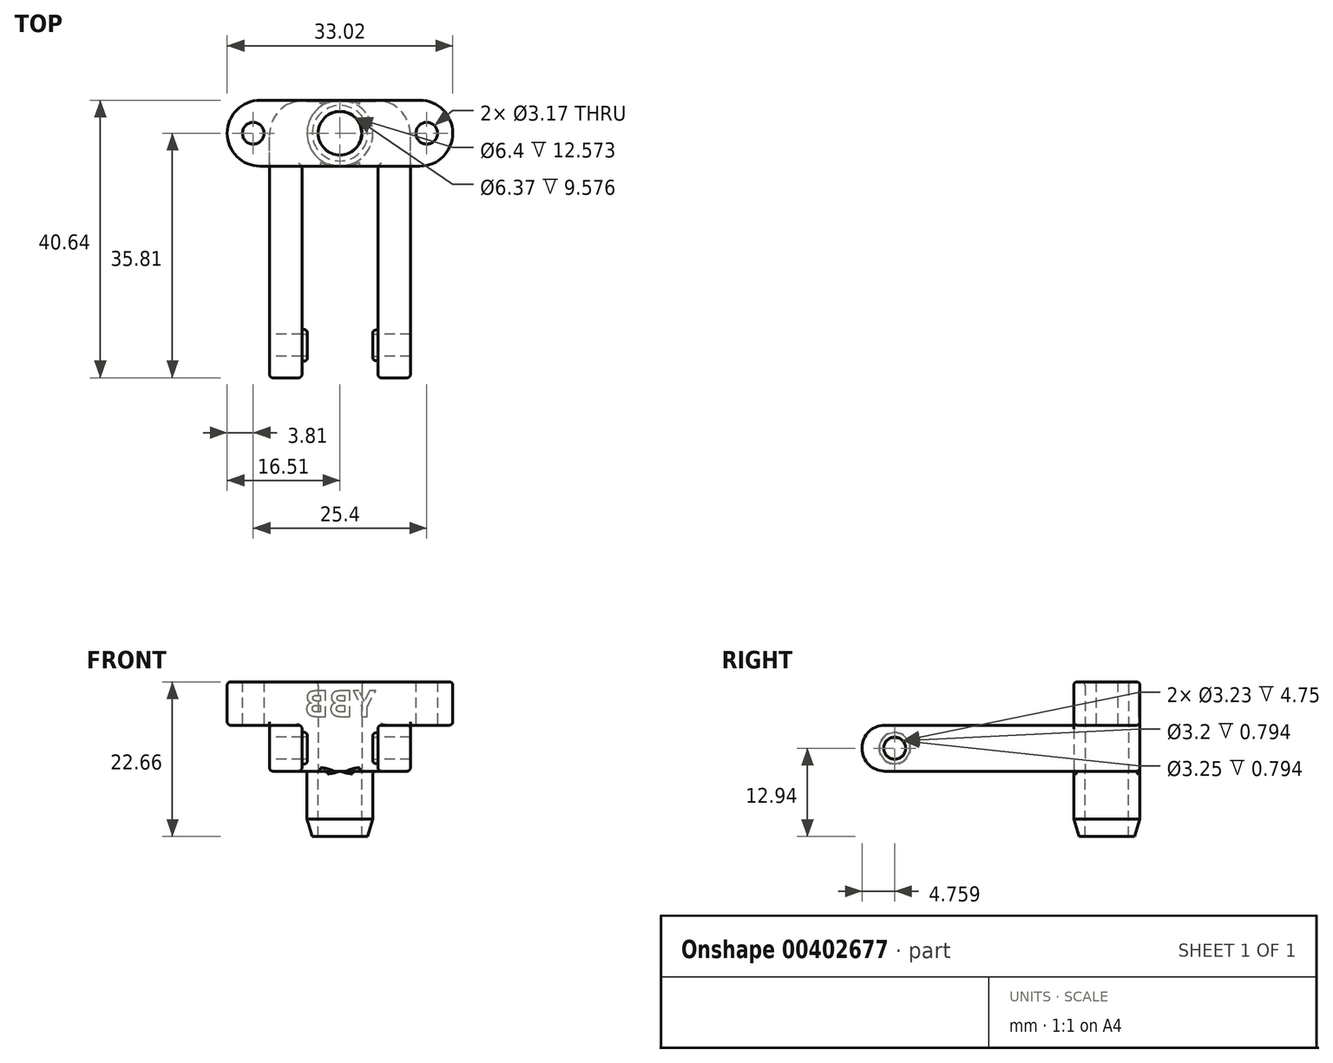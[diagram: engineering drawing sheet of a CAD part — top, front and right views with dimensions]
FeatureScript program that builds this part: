
annotation { "Feature Type Name" : "Feature", "Feature Type Description" : "" }
export const myFeature = defineFeature(function(context is Context, id is Id, definition is map)
    precondition{}
    {
        {
            var Q0;
            Q0=qCreatedBy(makeId("Top.planeOp"),FACE);
            var sketch = newSketch(context, id + "F0", { "sketchPlane" : qUnion([Q0])});
            skLineSegment(sketch, "E0.bottom", {"start": v(10.31, -4.83) * mm, "end": v(-10.31, -4.83) * mm});
            skLineSegment(sketch, "E0.top", {"start": v(10.31, 4.83) * mm, "end": v(-10.31, 4.83) * mm});
            skLineSegment(sketch, "E0.left", {"start": v(10.31, -4.83) * mm, "end": v(10.31, 4.83) * mm});
            skLineSegment(sketch, "E0.right", {"start": v(-10.31, -4.83) * mm, "end": v(-10.31, 4.83) * mm});
            skPoint(sketch, "E0.middle", {"position": v(0, 0) * mm});
            skCircle(sketch, "E1", {"center": v(0, 0) * mm, "radius": 3.2 * mm});
            skLineSegment(sketch, "E2.bottom", {"start": v(10.31, -4.83) * mm, "end": v(5.56, -4.83) * mm});
            skLineSegment(sketch, "E2.top", {"start": v(10.31, -35.81) * mm, "end": v(5.56, -35.81) * mm});
            skLineSegment(sketch, "E2.left", {"start": v(10.31, -4.83) * mm, "end": v(10.31, -35.81) * mm});
            skLineSegment(sketch, "E2.right", {"start": v(5.56, -4.83) * mm, "end": v(5.56, -35.81) * mm});
            skLineSegment(sketch, "E3.MirrorCS", {"start": v(-5.56, -4.83) * mm, "end": v(-5.56, -35.81) * mm});
            skLineSegment(sketch, "E4.MirrorCS", {"start": v(-10.31, -35.81) * mm, "end": v(-5.56, -35.81) * mm});
            skLineSegment(sketch, "E5.MirrorCS", {"start": v(-10.31, -4.83) * mm, "end": v(-10.31, -35.81) * mm});
            skSolve(sketch);
        }
        {
            var Q0;
            {var subQ8=sQuery(id+"F0.wireOp",EDGE,"E3.MirrorCS");Q0=qUnion([makeQuery(id+"F0.imprint","IMPRINT",FACE,{"disambiguationData":[TD([[makeQuery(id+"F0.imprint","IMPRINT",EDGE,{"derivedFrom":sQuery(id+"F0.wireOp",EDGE,"E0.top")}),1.0]])]}),makeQuery(id+"F0.imprint","IMPRINT",FACE,{"disambiguationData":[TD([[makeQuery(id+"F0.imprint","IMPRINT",EDGE,{"derivedFrom":subQ8}),-1.0]])]}),makeQuery(id+"F0.imprint","IMPRINT",FACE,{"disambiguationData":[TD([[makeQuery(id+"F0.imprint","IMPRINT",EDGE,{"derivedFrom":sQuery(id+"F0.wireOp",EDGE,"E2.top")}),-1.0]])]})]);}
            extrude(context, id + "F1", {"entities" : qUnion([Q0]), "endBound" : BoundingType.SYMMETRIC, "depth" : 6.73 * mm});
        }
        {
            var Q0;
            Q0=makeQuery(id+"F1.opExtrude","CAP_FACE",FACE,{"disambiguationData":[OSD([sQuery(id+"F0.wireOp",EDGE,"E0.bottom"),sQuery(id+"F0.wireOp",EDGE,"E0.top"),sQuery(id+"F0.wireOp",EDGE,"E0.left"),sQuery(id+"F0.wireOp",EDGE,"E0.right"),sQuery(id+"F0.wireOp",EDGE,"E1"),sQuery(id+"F0.wireOp",EDGE,"E2.top"),sQuery(id+"F0.wireOp",EDGE,"E2.left"),sQuery(id+"F0.wireOp",EDGE,"E2.right"),sQuery(id+"F0.wireOp",EDGE,"E3.MirrorCS"),sQuery(id+"F0.wireOp",EDGE,"E4.MirrorCS"),sQuery(id+"F0.wireOp",EDGE,"E5.MirrorCS")])],"isStart":true});
            var sketch = newSketch(context, id + "F2", { "sketchPlane" : qUnion([Q0])});
            skCircle(sketch, "E6", {"center": v(0, 0) * mm, "radius": 4.83 * mm});
            skCircle(sketch, "E7", {"center": v(0, 0) * mm, "radius": 3.15 * mm});
            skSolve(sketch);
        }
        {
            var Q0;
            Q0=makeQuery(id+"F1.opExtrude","SWEPT_FACE",FACE,{"disambiguationData":[OSD([sQuery(id+"F0.wireOp",EDGE,"E0.right"),sQuery(id+"F0.wireOp",EDGE,"E5.MirrorCS")])]});
            var sketch = newSketch(context, id + "F3", { "sketchPlane" : qUnion([Q0])});
            skCircle(sketch, "E8", {"center": v(31.05, 0) * mm, "radius": 1.61 * mm});
            skSolve(sketch);
        }
        {
            var Q0;
            Q0 = qSketchRegion(id + "F3", true);
            extrude(context, id + "F4", {"entities" : qUnion([Q0]), "operationType" : NewBodyOperationType.REMOVE, "endBound" : BoundingType.THROUGH_ALL, "oppositeDirection" : true, "depth" : 25.4 * mm});
        }
        {
            var Q0;
            Q0 = qSketchRegion(id + "F2", true);
            extrude(context, id + "F5", {"entities" : qUnion([Q0]), "operationType" : NewBodyOperationType.ADD, "depth" : 9.58 * mm});
        }
        {
            var Q0;
            Q0=makeQuery(id+"F1.opExtrude","SWEPT_FACE",FACE,{"disambiguationData":[OSD([sQuery(id+"F0.wireOp",EDGE,"E3.MirrorCS")])]});
            var sketch = newSketch(context, id + "F6", { "sketchPlane" : qUnion([Q0])});
            skCircle(sketch, "E9", {"center": v(-31.05, 0) * mm, "radius": 1.6 * mm});
            skCircle(sketch, "E10", {"center": v(-31.05, 0) * mm, "radius": 2.32 * mm});
            skSolve(sketch);
        }
        {
            var Q0;
            Q0 = qSketchRegion(id + "F6", true);
            extrude(context, id + "F7", {"entities" : qUnion([Q0]), "operationType" : NewBodyOperationType.ADD, "depth" : 0.8 * mm});
        }
        {
            var Q0;
            Q0=makeQuery(id+"F1.opExtrude","SWEPT_FACE",FACE,{"disambiguationData":[OSD([sQuery(id+"F0.wireOp",EDGE,"E2.right")])]});
            var sketch = newSketch(context, id + "F8", { "sketchPlane" : qUnion([Q0])});
            skCircle(sketch, "E11", {"center": v(31.05, 0) * mm, "radius": 1.62 * mm});
            skCircle(sketch, "E12", {"center": v(31.05, 0) * mm, "radius": 2.25 * mm});
            skSolve(sketch);
        }
        {
            var Q0;
            Q0 = qSketchRegion(id + "F8", true);
            extrude(context, id + "F9", {"entities" : qUnion([Q0]), "operationType" : NewBodyOperationType.ADD, "depth" : 0.8 * mm});
        }
        {
            var Q0;
            Q0=makeQuery(id+"F1.opExtrude","CAP_FACE",FACE,{"disambiguationData":[OSD([sQuery(id+"F0.wireOp",EDGE,"E0.bottom"),sQuery(id+"F0.wireOp",EDGE,"E0.top"),sQuery(id+"F0.wireOp",EDGE,"E0.left"),sQuery(id+"F0.wireOp",EDGE,"E0.right"),sQuery(id+"F0.wireOp",EDGE,"E1"),sQuery(id+"F0.wireOp",EDGE,"E2.top"),sQuery(id+"F0.wireOp",EDGE,"E2.left"),sQuery(id+"F0.wireOp",EDGE,"E2.right"),sQuery(id+"F0.wireOp",EDGE,"E3.MirrorCS"),sQuery(id+"F0.wireOp",EDGE,"E4.MirrorCS"),sQuery(id+"F0.wireOp",EDGE,"E5.MirrorCS")])],"isStart":false});
            var sketch = newSketch(context, id + "F10", { "sketchPlane" : qUnion([Q0])});
            skLineSegment(sketch, "E13.bottom", {"start": v(16.51, -4.83) * mm, "end": v(-16.51, -4.83) * mm});
            skLineSegment(sketch, "E13.top", {"start": v(16.51, 4.83) * mm, "end": v(-16.51, 4.83) * mm});
            skLineSegment(sketch, "E13.left", {"start": v(16.51, -4.83) * mm, "end": v(16.51, 4.83) * mm});
            skLineSegment(sketch, "E13.right", {"start": v(-16.51, -4.83) * mm, "end": v(-16.51, 4.83) * mm});
            skPoint(sketch, "E13.middle", {"position": v(0, 0) * mm});
            skCircle(sketch, "E14", {"center": v(0, 0) * mm, "radius": 3.2 * mm});
            skCircle(sketch, "E15", {"center": v(12.7, 0) * mm, "radius": 1.59 * mm});
            skCircle(sketch, "E16.MirrorC", {"center": v(-12.7, 0) * mm, "radius": 1.59 * mm});
            skSolve(sketch);
        }
        {
            var Q0;
            Q0 = qSketchRegion(id + "F10", true);
            extrude(context, id + "F11", {"entities" : qUnion([Q0]), "operationType" : NewBodyOperationType.ADD, "depth" : 6.35 * mm});
        }
        {
            var Q0;
            Q0=makeQuery(id+"F11.opExtrude","CAP_EDGE",EDGE,{"disambiguationData":[OSD([sQuery(id+"F10.wireOp",EDGE,"E13.left")])],"isStart":false});
            var Q1;
            Q1=makeQuery(id+"F11.opExtrude","CAP_EDGE",EDGE,{"disambiguationData":[OSD([sQuery(id+"F10.wireOp",EDGE,"E13.top")])],"isStart":false});
            var Q2;
            Q2=makeQuery(id+"F11.opExtrude","CAP_EDGE",EDGE,{"disambiguationData":[OSD([sQuery(id+"F10.wireOp",EDGE,"E13.right")])],"isStart":false});
            var Q3;
            Q3=makeQuery(id+"F11.opExtrude","CAP_EDGE",EDGE,{"disambiguationData":[OSD([sQuery(id+"F10.wireOp",EDGE,"E13.bottom")])],"isStart":false});
            var Q4;
            Q4=makeQuery(id+"F11.opExtrude","CAP_EDGE",EDGE,{"disambiguationData":[OSD([sQuery(id+"F10.wireOp",EDGE,"E14")])],"isStart":false});
            var Q5;
            {var subQ2=sQuery(id+"F0.wireOp",EDGE,"E0.bottom");var subQ3=sQuery(id+"F10.wireOp",EDGE,"E13.bottom");var subQ4=makeQuery(id+"F11.opExtrude","SWEPT_FACE",FACE,{"disambiguationData":[OSD([subQ3])]});var subQ5=makeQuery(id+"F1.opExtrude","SWEPT_FACE",FACE,{"disambiguationData":[OSD([subQ2])]});var subQ6=sQuery(id+"F10.wireOp",EDGE,"E13.right");var subQ7=makeQuery(id+"F11.opExtrude","CAP_FACE",FACE,{"disambiguationData":[OSD([subQ3,sQuery(id+"F10.wireOp",EDGE,"E13.top"),sQuery(id+"F10.wireOp",EDGE,"E13.left"),subQ6,sQuery(id+"F10.wireOp",EDGE,"E14"),sQuery(id+"F10.wireOp",EDGE,"E15"),sQuery(id+"F10.wireOp",EDGE,"E16.MirrorC")])],"isStart":true});Q5=makeQuery(id+"F11.boolean.opBoolean","SPLIT",EDGE,{"disambiguationData":[topologyDisambiguationEdgeConnected([subQ5,subQ4,subQ7]),TD([makeQuery(id+"F11.opExtrude","SWEPT_FACE",FACE,{"disambiguationData":[OSD([subQ6])]})])],"derivedFrom":makeQuery(id+"F11.opExtrude","CAP_EDGE",EDGE,{"disambiguationData":[OSD([subQ3])],"isStart":true})});}
            var Q6;
            {var subQ2=sQuery(id+"F10.wireOp",EDGE,"E13.left");var subQ3=sQuery(id+"F10.wireOp",EDGE,"E13.bottom");var subQ4=makeQuery(id+"F11.opExtrude","CAP_FACE",FACE,{"disambiguationData":[OSD([subQ3,sQuery(id+"F10.wireOp",EDGE,"E13.top"),subQ2,sQuery(id+"F10.wireOp",EDGE,"E13.right"),sQuery(id+"F10.wireOp",EDGE,"E14"),sQuery(id+"F10.wireOp",EDGE,"E15"),sQuery(id+"F10.wireOp",EDGE,"E16.MirrorC")])],"isStart":true});var subQ5=sQuery(id+"F0.wireOp",EDGE,"E0.bottom");var subQ6=makeQuery(id+"F11.opExtrude","SWEPT_FACE",FACE,{"disambiguationData":[OSD([subQ3])]});var subQ7=makeQuery(id+"F1.opExtrude","SWEPT_FACE",FACE,{"disambiguationData":[OSD([subQ5])]});Q6=makeQuery(id+"F11.boolean.opBoolean","SPLIT",EDGE,{"disambiguationData":[topologyDisambiguationEdgeConnected([subQ7,subQ6,subQ4]),TD([makeQuery(id+"F11.opExtrude","SWEPT_FACE",FACE,{"disambiguationData":[OSD([subQ2])]})])],"derivedFrom":makeQuery(id+"F11.opExtrude","CAP_EDGE",EDGE,{"disambiguationData":[OSD([subQ3])],"isStart":true})});}
            var Q7;
            Q7=makeQuery(id+"F11.opExtrude","CAP_EDGE",EDGE,{"disambiguationData":[OSD([sQuery(id+"F10.wireOp",EDGE,"E13.left")])],"isStart":true});
            var Q8;
            {var subQ0=sQuery(id+"F10.wireOp",EDGE,"E13.top");var subQ1=sQuery(id+"F10.wireOp",EDGE,"E13.left");Q8=makeQuery(id+"F11.boolean.opBoolean","SPLIT",EDGE,{"disambiguationData":[TD([makeQuery(id+"F11.opExtrude","SWEPT_FACE",FACE,{"disambiguationData":[OSD([subQ1])]})])],"derivedFrom":makeQuery(id+"F11.opExtrude","CAP_EDGE",EDGE,{"disambiguationData":[OSD([subQ0])],"isStart":true})});}
            var Q9;
            {var subQ0=sQuery(id+"F10.wireOp",EDGE,"E13.top");var subQ1=sQuery(id+"F10.wireOp",EDGE,"E13.right");Q9=makeQuery(id+"F11.boolean.opBoolean","SPLIT",EDGE,{"disambiguationData":[TD([makeQuery(id+"F11.opExtrude","SWEPT_FACE",FACE,{"disambiguationData":[OSD([subQ1])]})])],"derivedFrom":makeQuery(id+"F11.opExtrude","CAP_EDGE",EDGE,{"disambiguationData":[OSD([subQ0])],"isStart":true})});}
            var Q10;
            Q10=makeQuery(id+"F11.opExtrude","CAP_EDGE",EDGE,{"disambiguationData":[OSD([sQuery(id+"F10.wireOp",EDGE,"E13.right")])],"isStart":true});
            fillet(context, id + "F12", {"entities" : qUnion([Q0, Q1, Q2, Q3, Q4, Q5, Q6, Q7, Q8, Q9, Q10]), "radius" : 0.5 * mm, "allowEdgeOverflow" : false});
        }
        {
            var Q0;
            Q0=makeQuery(id+"F1.opExtrude","CAP_EDGE",EDGE,{"disambiguationData":[OSD([sQuery(id+"F0.wireOp",EDGE,"E3.MirrorCS")])],"isStart":false});
            var Q1;
            Q1=makeQuery(id+"F7.opExtrude","CAP_EDGE",EDGE,{"disambiguationData":[OSD([sQuery(id+"F6.wireOp",EDGE,"E10")])],"isStart":false});
            var Q2;
            Q2=makeQuery(id+"F1.opExtrude","CAP_EDGE",EDGE,{"disambiguationData":[OSD([sQuery(id+"F0.wireOp",EDGE,"E2.right")])],"isStart":false});
            var Q3;
            Q3=makeQuery(id+"F9.opExtrude","CAP_EDGE",EDGE,{"disambiguationData":[OSD([sQuery(id+"F8.wireOp",EDGE,"E12")])],"isStart":false});
            fillet(context, id + "F13", {"entities" : qUnion([Q0, Q1, Q2, Q3]), "radius" : 0.5 * mm, "tangentPropagation" : true, "allowEdgeOverflow" : false});
        }
        {
            var Q0;
            Q0=makeQuery(id+"F5.boolean.opBoolean","SPLIT",EDGE,{"disambiguationData":[OD(0.0)],"derivedFrom":makeQuery(id+"F5.opExtrude","CAP_EDGE",EDGE,{"disambiguationData":[OSD([sQuery(id+"F2.wireOp",EDGE,"E6")])],"isStart":true})});
            var Q1;
            Q1=makeQuery(id+"F5.boolean.opBoolean","SPLIT",EDGE,{"disambiguationData":[OD(1.0)],"derivedFrom":makeQuery(id+"F5.opExtrude","CAP_EDGE",EDGE,{"disambiguationData":[OSD([sQuery(id+"F2.wireOp",EDGE,"E6")])],"isStart":true})});
            fillet(context, id + "F14", {"entities" : qUnion([Q0, Q1]), "radius" : 0.38 * mm, "tangentPropagation" : true, "allowEdgeOverflow" : false});
        }
        {
            var Q0;
            Q0=makeQuery(id+"F1.opExtrude","SWEPT_EDGE",EDGE,{"disambiguationData":[OSD([sQuery(id+"F0.wireOp",EDGE,"E3.MirrorCS"),sQuery(id+"F0.wireOp",EDGE,"E4.MirrorCS")])]});
            var Q1;
            Q1=makeQuery(id+"F1.opExtrude","SWEPT_EDGE",EDGE,{"disambiguationData":[OSD([sQuery(id+"F0.wireOp",EDGE,"E2.top"),sQuery(id+"F0.wireOp",EDGE,"E2.right")])]});
            var Q2;
            {var subQ0=sQuery(id+"F0.wireOp",EDGE,"E5.MirrorCS");var subQ1=sQuery(id+"F0.wireOp",EDGE,"E0.right");Q2=makeQuery(id+"F11.boolean.opBoolean","SPLIT",EDGE,{"disambiguationData":[topologyDisambiguationEdgeConnected([makeQuery(id+"F1.opExtrude","CAP_FACE",FACE,{"disambiguationData":[OSD([sQuery(id+"F0.wireOp",EDGE,"E0.bottom"),sQuery(id+"F0.wireOp",EDGE,"E0.top"),sQuery(id+"F0.wireOp",EDGE,"E0.left"),subQ1,sQuery(id+"F0.wireOp",EDGE,"E1"),sQuery(id+"F0.wireOp",EDGE,"E2.top"),sQuery(id+"F0.wireOp",EDGE,"E2.left"),sQuery(id+"F0.wireOp",EDGE,"E2.right"),sQuery(id+"F0.wireOp",EDGE,"E3.MirrorCS"),sQuery(id+"F0.wireOp",EDGE,"E4.MirrorCS"),subQ0])],"isStart":false})])],"derivedFrom":makeQuery(id+"F1.opExtrude","CAP_EDGE",EDGE,{"disambiguationData":[OSD([subQ1,subQ0])],"isStart":false})});}
            var Q3;
            Q3=makeQuery(id+"F1.opExtrude","SWEPT_EDGE",EDGE,{"disambiguationData":[OSD([sQuery(id+"F0.wireOp",EDGE,"E4.MirrorCS"),sQuery(id+"F0.wireOp",EDGE,"E5.MirrorCS")])]});
            var Q4;
            Q4=makeQuery(id+"F1.opExtrude","CAP_EDGE",EDGE,{"disambiguationData":[OSD([sQuery(id+"F0.wireOp",EDGE,"E0.right"),sQuery(id+"F0.wireOp",EDGE,"E5.MirrorCS")])],"isStart":true});
            var Q5;
            {var subQ0=sQuery(id+"F0.wireOp",EDGE,"E5.MirrorCS");var subQ1=sQuery(id+"F0.wireOp",EDGE,"E0.right");var subQ2=sQuery(id+"F0.wireOp",EDGE,"E0.top");Q5=makeQuery(id+"F5.boolean.opBoolean","SPLIT",EDGE,{"disambiguationData":[TD([makeQuery(id+"F1.opExtrude","SWEPT_FACE",FACE,{"disambiguationData":[OSD([subQ1,subQ0])]})])],"derivedFrom":makeQuery(id+"F1.opExtrude","CAP_EDGE",EDGE,{"disambiguationData":[OSD([subQ2])],"isStart":true})});}
            var Q6;
            {var subQ0=sQuery(id+"F0.wireOp",EDGE,"E2.left");var subQ1=sQuery(id+"F0.wireOp",EDGE,"E0.left");var subQ2=sQuery(id+"F0.wireOp",EDGE,"E0.top");Q6=makeQuery(id+"F5.boolean.opBoolean","SPLIT",EDGE,{"disambiguationData":[TD([makeQuery(id+"F1.opExtrude","SWEPT_FACE",FACE,{"disambiguationData":[OSD([subQ1,subQ0])]})])],"derivedFrom":makeQuery(id+"F1.opExtrude","CAP_EDGE",EDGE,{"disambiguationData":[OSD([subQ2])],"isStart":true})});}
            var Q7;
            {var subQ0=sQuery(id+"F0.wireOp",EDGE,"E0.bottom");var subQ1=sQuery(id+"F0.wireOp",EDGE,"E3.MirrorCS");Q7=makeQuery(id+"F5.boolean.opBoolean","SPLIT",EDGE,{"disambiguationData":[TD([makeQuery(id+"F1.opExtrude","SWEPT_FACE",FACE,{"disambiguationData":[OSD([subQ1])]})])],"derivedFrom":makeQuery(id+"F1.opExtrude","CAP_EDGE",EDGE,{"disambiguationData":[OSD([subQ0])],"isStart":true})});}
            var Q8;
            Q8=makeQuery(id+"F1.opExtrude","CAP_EDGE",EDGE,{"disambiguationData":[OSD([sQuery(id+"F0.wireOp",EDGE,"E3.MirrorCS")])],"isStart":true});
            var Q9;
            {var subQ0=sQuery(id+"F0.wireOp",EDGE,"E0.bottom");var subQ1=sQuery(id+"F0.wireOp",EDGE,"E2.right");Q9=makeQuery(id+"F5.boolean.opBoolean","SPLIT",EDGE,{"disambiguationData":[TD([makeQuery(id+"F1.opExtrude","SWEPT_FACE",FACE,{"disambiguationData":[OSD([subQ1])]})])],"derivedFrom":makeQuery(id+"F1.opExtrude","CAP_EDGE",EDGE,{"disambiguationData":[OSD([subQ0])],"isStart":true})});}
            var Q10;
            Q10=makeQuery(id+"F1.opExtrude","CAP_EDGE",EDGE,{"disambiguationData":[OSD([sQuery(id+"F0.wireOp",EDGE,"E2.right")])],"isStart":true});
            var Q11;
            Q11=makeQuery(id+"F1.opExtrude","CAP_EDGE",EDGE,{"disambiguationData":[OSD([sQuery(id+"F0.wireOp",EDGE,"E0.left"),sQuery(id+"F0.wireOp",EDGE,"E2.left")])],"isStart":true});
            var Q12;
            Q12=makeQuery(id+"F1.opExtrude","SWEPT_EDGE",EDGE,{"disambiguationData":[OSD([sQuery(id+"F0.wireOp",EDGE,"E2.top"),sQuery(id+"F0.wireOp",EDGE,"E2.left")])]});
            var Q13;
            {var subQ0=sQuery(id+"F0.wireOp",EDGE,"E2.left");var subQ1=sQuery(id+"F0.wireOp",EDGE,"E0.left");Q13=makeQuery(id+"F11.boolean.opBoolean","SPLIT",EDGE,{"disambiguationData":[topologyDisambiguationEdgeConnected([makeQuery(id+"F1.opExtrude","CAP_FACE",FACE,{"disambiguationData":[OSD([sQuery(id+"F0.wireOp",EDGE,"E0.bottom"),sQuery(id+"F0.wireOp",EDGE,"E0.top"),subQ1,sQuery(id+"F0.wireOp",EDGE,"E0.right"),sQuery(id+"F0.wireOp",EDGE,"E1"),sQuery(id+"F0.wireOp",EDGE,"E2.top"),subQ0,sQuery(id+"F0.wireOp",EDGE,"E2.right"),sQuery(id+"F0.wireOp",EDGE,"E3.MirrorCS"),sQuery(id+"F0.wireOp",EDGE,"E4.MirrorCS"),sQuery(id+"F0.wireOp",EDGE,"E5.MirrorCS")])],"isStart":false})])],"derivedFrom":makeQuery(id+"F1.opExtrude","CAP_EDGE",EDGE,{"disambiguationData":[OSD([subQ1,subQ0])],"isStart":false})});}
            fillet(context, id + "F15", {"entities" : qUnion([Q0, Q1, Q2, Q3, Q4, Q5, Q6, Q7, Q8, Q9, Q10, Q11, Q12, Q13]), "radius" : 0.5 * mm, "allowEdgeOverflow" : false});
        }
        {
            var Q0;
            Q0=makeQuery(id+"F1.opExtrude","CAP_EDGE",EDGE,{"disambiguationData":[OSD([sQuery(id+"F0.wireOp",EDGE,"E4.MirrorCS")])],"isStart":true});
            var Q1;
            Q1=makeQuery(id+"F1.opExtrude","CAP_EDGE",EDGE,{"disambiguationData":[OSD([sQuery(id+"F0.wireOp",EDGE,"E2.top")])],"isStart":true});
            var Q2;
            Q2=makeQuery(id+"F1.opExtrude","CAP_EDGE",EDGE,{"disambiguationData":[OSD([sQuery(id+"F0.wireOp",EDGE,"E2.top")])],"isStart":false});
            var Q3;
            Q3=makeQuery(id+"F1.opExtrude","CAP_EDGE",EDGE,{"disambiguationData":[OSD([sQuery(id+"F0.wireOp",EDGE,"E4.MirrorCS")])],"isStart":false});
            fillet(context, id + "F16", {"entities" : qUnion([Q0, Q1, Q2, Q3]), "radius" : 3.3 * mm, "tangentPropagation" : true, "allowEdgeOverflow" : false});
        }
        {
            var Q0;
            Q0=makeQuery(id+"F11.opExtrude","SWEPT_EDGE",EDGE,{"disambiguationData":[OSD([sQuery(id+"F10.wireOp",EDGE,"E13.bottom"),sQuery(id+"F10.wireOp",EDGE,"E13.right")])]});
            var Q1;
            Q1=makeQuery(id+"F11.opExtrude","SWEPT_EDGE",EDGE,{"disambiguationData":[OSD([sQuery(id+"F10.wireOp",EDGE,"E13.top"),sQuery(id+"F10.wireOp",EDGE,"E13.right")])]});
            var Q2;
            Q2=makeQuery(id+"F11.opExtrude","SWEPT_EDGE",EDGE,{"disambiguationData":[OSD([sQuery(id+"F10.wireOp",EDGE,"E13.top"),sQuery(id+"F10.wireOp",EDGE,"E13.left")])]});
            var Q3;
            Q3=makeQuery(id+"F11.opExtrude","SWEPT_EDGE",EDGE,{"disambiguationData":[OSD([sQuery(id+"F10.wireOp",EDGE,"E13.bottom"),sQuery(id+"F10.wireOp",EDGE,"E13.left")])]});
            fillet(context, id + "F17", {"entities" : qUnion([Q0, Q1, Q2, Q3]), "radius" : 4.83 * mm, "tangentPropagation" : true, "allowEdgeOverflow" : false});
        }
        {
            var Q0;
            Q0=makeQuery(id+"F1.opExtrude","SWEPT_EDGE",EDGE,{"disambiguationData":[OSD([sQuery(id+"F0.wireOp",EDGE,"E0.top"),sQuery(id+"F0.wireOp",EDGE,"E0.left")])]});
            var Q1;
            Q1=makeQuery(id+"F1.opExtrude","SWEPT_EDGE",EDGE,{"disambiguationData":[OSD([sQuery(id+"F0.wireOp",EDGE,"E0.top"),sQuery(id+"F0.wireOp",EDGE,"E0.right")])]});
            fillet(context, id + "F18", {"entities" : qUnion([Q0, Q1]), "radius" : 5.08 * mm, "tangentPropagation" : true, "allowEdgeOverflow" : false});
        }
        {
            var Q0;
            Q0=makeQuery(id+"F5.opExtrude","CAP_EDGE",EDGE,{"disambiguationData":[OSD([sQuery(id+"F2.wireOp",EDGE,"E6")])],"isStart":false});
            chamfer(context, id + "F19", {"entities" : qUnion([Q0]), "chamferType" : ChamferType.TWO_OFFSETS, "width1" : 0.76 * mm, "oppositeDirection" : false, "width2" : 2.54 * mm, "tangentPropagation" : true});
        }
        {
            var Q0;
            Q0=makeQuery(id+"F11.opExtrude","CAP_FACE",FACE,{"disambiguationData":[OSD([sQuery(id+"F10.wireOp",EDGE,"E13.bottom"),sQuery(id+"F10.wireOp",EDGE,"E13.top"),sQuery(id+"F10.wireOp",EDGE,"E13.left"),sQuery(id+"F10.wireOp",EDGE,"E13.right"),sQuery(id+"F10.wireOp",EDGE,"E14"),sQuery(id+"F10.wireOp",EDGE,"E15"),sQuery(id+"F10.wireOp",EDGE,"E16.MirrorC")])],"isStart":false});
            var sketch = newSketch(context, id + "F20", { "sketchPlane" : qUnion([Q0])});
            skCircle(sketch, "E17", {"center": v(0, 0) * mm, "radius": 3.18 * mm});
            skSolve(sketch);
        }
        {
            var Q0;
            Q0 = qSketchRegion(id + "F20", true);
            extrude(context, id + "F21", {"entities" : qUnion([Q0]), "operationType" : NewBodyOperationType.REMOVE, "oppositeDirection" : true, "depth" : 38.1 * mm});
        }
        {
            var Q0;
            Q0=makeQuery(id+"F11.boolean.opBoolean","MERGE",FACE,{"derivedFrom":[makeQuery(id+"F1.opExtrude","SWEPT_FACE",FACE,{"disambiguationData":[OSD([sQuery(id+"F0.wireOp",EDGE,"E0.top")])]}),makeQuery(id+"F11.opExtrude","SWEPT_FACE",FACE,{"disambiguationData":[OSD([sQuery(id+"F10.wireOp",EDGE,"E13.top")])]})]});
            var sketch = newSketch(context, id + "F22", { "sketchPlane" : qUnion([Q0])});
            skText(sketch, "E18", { "text": "YBB", "fontName": "OpenSans-Bold.ttf"});
            const initialGuessF22  = {"E18": [-0.00522, 0.00464, 1, 0, 0.0038]};
            skSetInitialGuess(sketch, initialGuessF22);
            skSolve(sketch);
        }
        {
            var Q0;
            Q0 = qSketchRegion(id + "F22", true);
            extrude(context, id + "F23", {"entities" : qUnion([Q0]), "operationType" : NewBodyOperationType.REMOVE, "oppositeDirection" : true, "depth" : 0.15 * mm});
        }
    });
